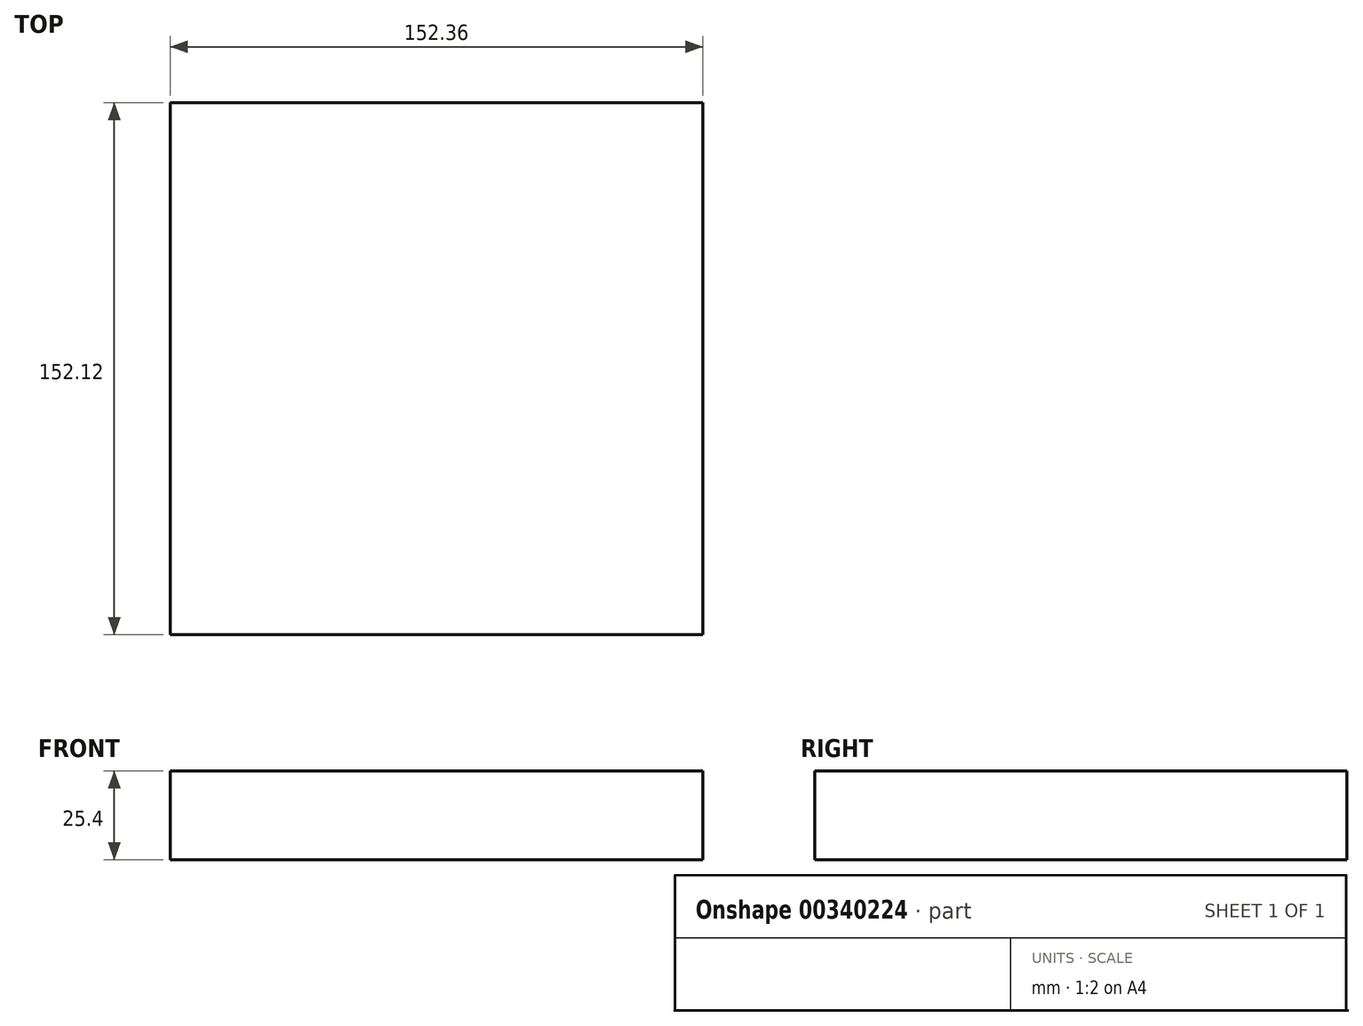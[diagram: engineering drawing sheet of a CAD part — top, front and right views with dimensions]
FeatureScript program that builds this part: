
annotation { "Feature Type Name" : "Feature", "Feature Type Description" : "" }
export const myFeature = defineFeature(function(context is Context, id is Id, definition is map)
    precondition{}
    {
        {
            var Q0;
            Q0=qCreatedBy(makeId("Top.planeOp"),FACE);
            var sketch = newSketch(context, id + "F0", { "sketchPlane" : qUnion([Q0])});
            skLineSegment(sketch, "E0.bottom", {"start": v(76.18, 76.06) * mm, "end": v(-76.18, 76.06) * mm});
            skLineSegment(sketch, "E0.top", {"start": v(76.18, -76.06) * mm, "end": v(-76.18, -76.06) * mm});
            skLineSegment(sketch, "E0.left", {"start": v(76.18, 76.06) * mm, "end": v(76.18, -76.06) * mm});
            skLineSegment(sketch, "E0.right", {"start": v(-76.18, 76.06) * mm, "end": v(-76.18, -76.06) * mm});
            skPoint(sketch, "E0.middle", {"position": v(0, 0) * mm});
            skSolve(sketch);
        }
        {
            var Q0;
            Q0=makeQuery(id+"F0.imprint","IMPRINT",FACE,{"disambiguationData":[TD([[makeQuery(id+"F0.imprint","IMPRINT",EDGE,{"derivedFrom":sQuery(id+"F0.wireOp",EDGE,"E0.bottom")}),1.0]])]});
            extrude(context, id + "F1", {"entities" : qUnion([Q0]), "depth" : 25.4 * mm});
        }
    });
